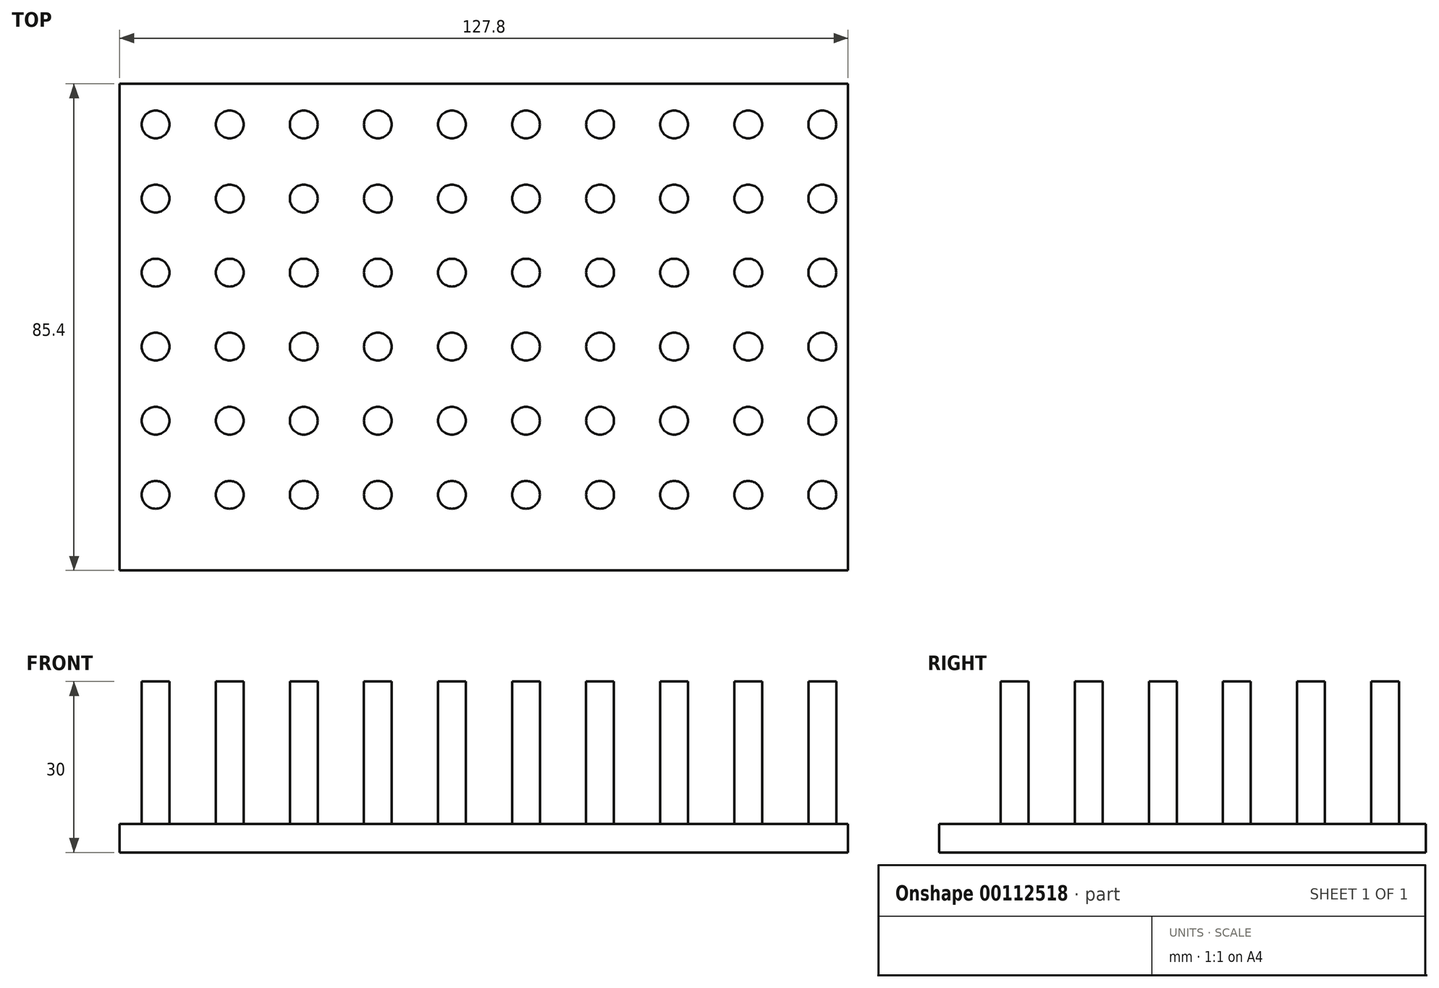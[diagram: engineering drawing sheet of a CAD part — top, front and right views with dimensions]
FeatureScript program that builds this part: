
annotation { "Feature Type Name" : "Feature", "Feature Type Description" : "" }
export const myFeature = defineFeature(function(context is Context, id is Id, definition is map)
    precondition{}
    {
        {
            var Q0;
            Q0=qCreatedBy(makeId("Top.planeOp"),FACE);
            var sketch = newSketch(context, id + "F0", { "sketchPlane" : qUnion([Q0])});
            skLineSegment(sketch, "E0.bottom", {"start": v(63.9, -42.7) * mm, "end": v(-63.9, -42.7) * mm});
            skLineSegment(sketch, "E0.top", {"start": v(63.9, 42.7) * mm, "end": v(-63.9, 42.7) * mm});
            skLineSegment(sketch, "E0.left", {"start": v(63.9, -42.7) * mm, "end": v(63.9, 42.7) * mm});
            skLineSegment(sketch, "E0.right", {"start": v(-63.9, -42.7) * mm, "end": v(-63.9, 42.7) * mm});
            skPoint(sketch, "E0.middle", {"position": v(0, 0) * mm});
            skSolve(sketch);
        }
        {
            var Q0;
            Q0 = qSketchRegion(id + "F0", true);
            extrude(context, id + "F1", {"entities" : qUnion([Q0]), "depth" : 5 * mm});
        }
        {
            var Q0;
            Q0=makeQuery(id+"F1.opExtrude","CAP_FACE",FACE,{"disambiguationData":[OSD([sQuery(id+"F0.wireOp",EDGE,"E0.bottom"),sQuery(id+"F0.wireOp",EDGE,"E0.top"),sQuery(id+"F0.wireOp",EDGE,"E0.left"),sQuery(id+"F0.wireOp",EDGE,"E0.right")])],"isStart":false});
            var sketch = newSketch(context, id + "F2", { "sketchPlane" : qUnion([Q0])});
            skCircle(sketch, "E1", {"center": v(-57.6, 35.56) * mm, "radius": 2.44 * mm});
            skCircle(sketch, "E2.1.0.0", {"center": v(-44.6, 35.56) * mm, "radius": 2.44 * mm});
            skCircle(sketch, "E2.2.0.0", {"center": v(-31.6, 35.56) * mm, "radius": 2.44 * mm});
            skCircle(sketch, "E2.3.0.0", {"center": v(-18.6, 35.56) * mm, "radius": 2.44 * mm});
            skCircle(sketch, "E2.4.0.0", {"center": v(-5.6, 35.56) * mm, "radius": 2.44 * mm});
            skCircle(sketch, "E2.5.0.0", {"center": v(7.4, 35.56) * mm, "radius": 2.44 * mm});
            skCircle(sketch, "E2.6.0.0", {"center": v(20.4, 35.56) * mm, "radius": 2.44 * mm});
            skCircle(sketch, "E2.7.0.0", {"center": v(33.4, 35.56) * mm, "radius": 2.44 * mm});
            skCircle(sketch, "E2.8.0.0", {"center": v(46.4, 35.56) * mm, "radius": 2.44 * mm});
            skCircle(sketch, "E2.9.0.0", {"center": v(59.4, 35.56) * mm, "radius": 2.44 * mm});
            skLineSegment(sketch, "E2.direction1", {"start": v(-57.6, 35.56) * mm, "end": v(-44.6, 35.56) * mm, "construction": true});
            skCircle(sketch, "E3.0.1.0", {"center": v(46.4, 22.56) * mm, "radius": 2.44 * mm});
            skCircle(sketch, "E3.0.1.1", {"center": v(33.4, 22.56) * mm, "radius": 2.44 * mm});
            skCircle(sketch, "E3.0.1.2", {"center": v(59.4, 22.56) * mm, "radius": 2.44 * mm});
            skLineSegment(sketch, "E3.0.1.3", {"start": v(-57.6, 22.56) * mm, "end": v(-44.6, 22.56) * mm, "construction": true});
            skCircle(sketch, "E3.0.1.4", {"center": v(-57.6, 22.56) * mm, "radius": 2.44 * mm});
            skCircle(sketch, "E3.0.1.5", {"center": v(-44.6, 22.56) * mm, "radius": 2.44 * mm});
            skCircle(sketch, "E3.0.1.6", {"center": v(-31.6, 22.56) * mm, "radius": 2.44 * mm});
            skCircle(sketch, "E3.0.1.7", {"center": v(-18.6, 22.56) * mm, "radius": 2.44 * mm});
            skCircle(sketch, "E3.0.1.8", {"center": v(-5.6, 22.56) * mm, "radius": 2.44 * mm});
            skCircle(sketch, "E3.0.1.9", {"center": v(7.4, 22.56) * mm, "radius": 2.44 * mm});
            skCircle(sketch, "E3.0.1.10", {"center": v(20.4, 22.56) * mm, "radius": 2.44 * mm});
            skCircle(sketch, "E3.0.2.0", {"center": v(46.4, 9.56) * mm, "radius": 2.44 * mm});
            skCircle(sketch, "E3.0.2.1", {"center": v(33.4, 9.56) * mm, "radius": 2.44 * mm});
            skCircle(sketch, "E3.0.2.2", {"center": v(59.4, 9.56) * mm, "radius": 2.44 * mm});
            skLineSegment(sketch, "E3.0.2.3", {"start": v(-57.6, 9.56) * mm, "end": v(-44.6, 9.56) * mm, "construction": true});
            skCircle(sketch, "E3.0.2.4", {"center": v(-57.6, 9.56) * mm, "radius": 2.44 * mm});
            skCircle(sketch, "E3.0.2.5", {"center": v(-44.6, 9.56) * mm, "radius": 2.44 * mm});
            skCircle(sketch, "E3.0.2.6", {"center": v(-31.6, 9.56) * mm, "radius": 2.44 * mm});
            skCircle(sketch, "E3.0.2.7", {"center": v(-18.6, 9.56) * mm, "radius": 2.44 * mm});
            skCircle(sketch, "E3.0.2.8", {"center": v(-5.6, 9.56) * mm, "radius": 2.44 * mm});
            skCircle(sketch, "E3.0.2.9", {"center": v(7.4, 9.56) * mm, "radius": 2.44 * mm});
            skCircle(sketch, "E3.0.2.10", {"center": v(20.4, 9.56) * mm, "radius": 2.44 * mm});
            skCircle(sketch, "E3.0.3.0", {"center": v(46.4, -3.44) * mm, "radius": 2.44 * mm});
            skCircle(sketch, "E3.0.3.1", {"center": v(33.4, -3.44) * mm, "radius": 2.44 * mm});
            skCircle(sketch, "E3.0.3.2", {"center": v(59.4, -3.44) * mm, "radius": 2.44 * mm});
            skLineSegment(sketch, "E3.0.3.3", {"start": v(-57.6, -3.44) * mm, "end": v(-44.6, -3.44) * mm, "construction": true});
            skCircle(sketch, "E3.0.3.4", {"center": v(-57.6, -3.44) * mm, "radius": 2.44 * mm});
            skCircle(sketch, "E3.0.3.5", {"center": v(-44.6, -3.44) * mm, "radius": 2.44 * mm});
            skCircle(sketch, "E3.0.3.6", {"center": v(-31.6, -3.44) * mm, "radius": 2.44 * mm});
            skCircle(sketch, "E3.0.3.7", {"center": v(-18.6, -3.44) * mm, "radius": 2.44 * mm});
            skCircle(sketch, "E3.0.3.8", {"center": v(-5.6, -3.44) * mm, "radius": 2.44 * mm});
            skCircle(sketch, "E3.0.3.9", {"center": v(7.4, -3.44) * mm, "radius": 2.44 * mm});
            skCircle(sketch, "E3.0.3.10", {"center": v(20.4, -3.44) * mm, "radius": 2.44 * mm});
            skCircle(sketch, "E3.0.4.0", {"center": v(46.4, -16.44) * mm, "radius": 2.44 * mm});
            skCircle(sketch, "E3.0.4.1", {"center": v(33.4, -16.44) * mm, "radius": 2.44 * mm});
            skCircle(sketch, "E3.0.4.2", {"center": v(59.4, -16.44) * mm, "radius": 2.44 * mm});
            skLineSegment(sketch, "E3.0.4.3", {"start": v(-57.6, -16.44) * mm, "end": v(-44.6, -16.44) * mm, "construction": true});
            skCircle(sketch, "E3.0.4.4", {"center": v(-57.6, -16.44) * mm, "radius": 2.44 * mm});
            skCircle(sketch, "E3.0.4.5", {"center": v(-44.6, -16.44) * mm, "radius": 2.44 * mm});
            skCircle(sketch, "E3.0.4.6", {"center": v(-31.6, -16.44) * mm, "radius": 2.44 * mm});
            skCircle(sketch, "E3.0.4.7", {"center": v(-18.6, -16.44) * mm, "radius": 2.44 * mm});
            skCircle(sketch, "E3.0.4.8", {"center": v(-5.6, -16.44) * mm, "radius": 2.44 * mm});
            skCircle(sketch, "E3.0.4.9", {"center": v(7.4, -16.44) * mm, "radius": 2.44 * mm});
            skCircle(sketch, "E3.0.4.10", {"center": v(20.4, -16.44) * mm, "radius": 2.44 * mm});
            skCircle(sketch, "E3.0.5.0", {"center": v(46.4, -29.44) * mm, "radius": 2.44 * mm});
            skCircle(sketch, "E3.0.5.1", {"center": v(33.4, -29.44) * mm, "radius": 2.44 * mm});
            skCircle(sketch, "E3.0.5.2", {"center": v(59.4, -29.44) * mm, "radius": 2.44 * mm});
            skLineSegment(sketch, "E3.0.5.3", {"start": v(-57.6, -29.44) * mm, "end": v(-44.6, -29.44) * mm, "construction": true});
            skCircle(sketch, "E3.0.5.4", {"center": v(-57.6, -29.44) * mm, "radius": 2.44 * mm});
            skCircle(sketch, "E3.0.5.5", {"center": v(-44.6, -29.44) * mm, "radius": 2.44 * mm});
            skCircle(sketch, "E3.0.5.6", {"center": v(-31.6, -29.44) * mm, "radius": 2.44 * mm});
            skCircle(sketch, "E3.0.5.7", {"center": v(-18.6, -29.44) * mm, "radius": 2.44 * mm});
            skCircle(sketch, "E3.0.5.8", {"center": v(-5.6, -29.44) * mm, "radius": 2.44 * mm});
            skCircle(sketch, "E3.0.5.9", {"center": v(7.4, -29.44) * mm, "radius": 2.44 * mm});
            skCircle(sketch, "E3.0.5.10", {"center": v(20.4, -29.44) * mm, "radius": 2.44 * mm});
            skLineSegment(sketch, "E3.direction1", {"start": v(-57.6, 35.56) * mm, "end": v(-32.6, 35.56) * mm, "construction": true});
            skLineSegment(sketch, "E3.direction2", {"start": v(-57.6, 35.56) * mm, "end": v(-57.6, 22.56) * mm, "construction": true});
            skSolve(sketch);
        }
        {
            var Q0;
            Q0 = qSketchRegion(id + "F2", true);
            extrude(context, id + "F3", {"entities" : qUnion([Q0]), "operationType" : NewBodyOperationType.ADD, "depth" : 25 * mm});
        }
    });
